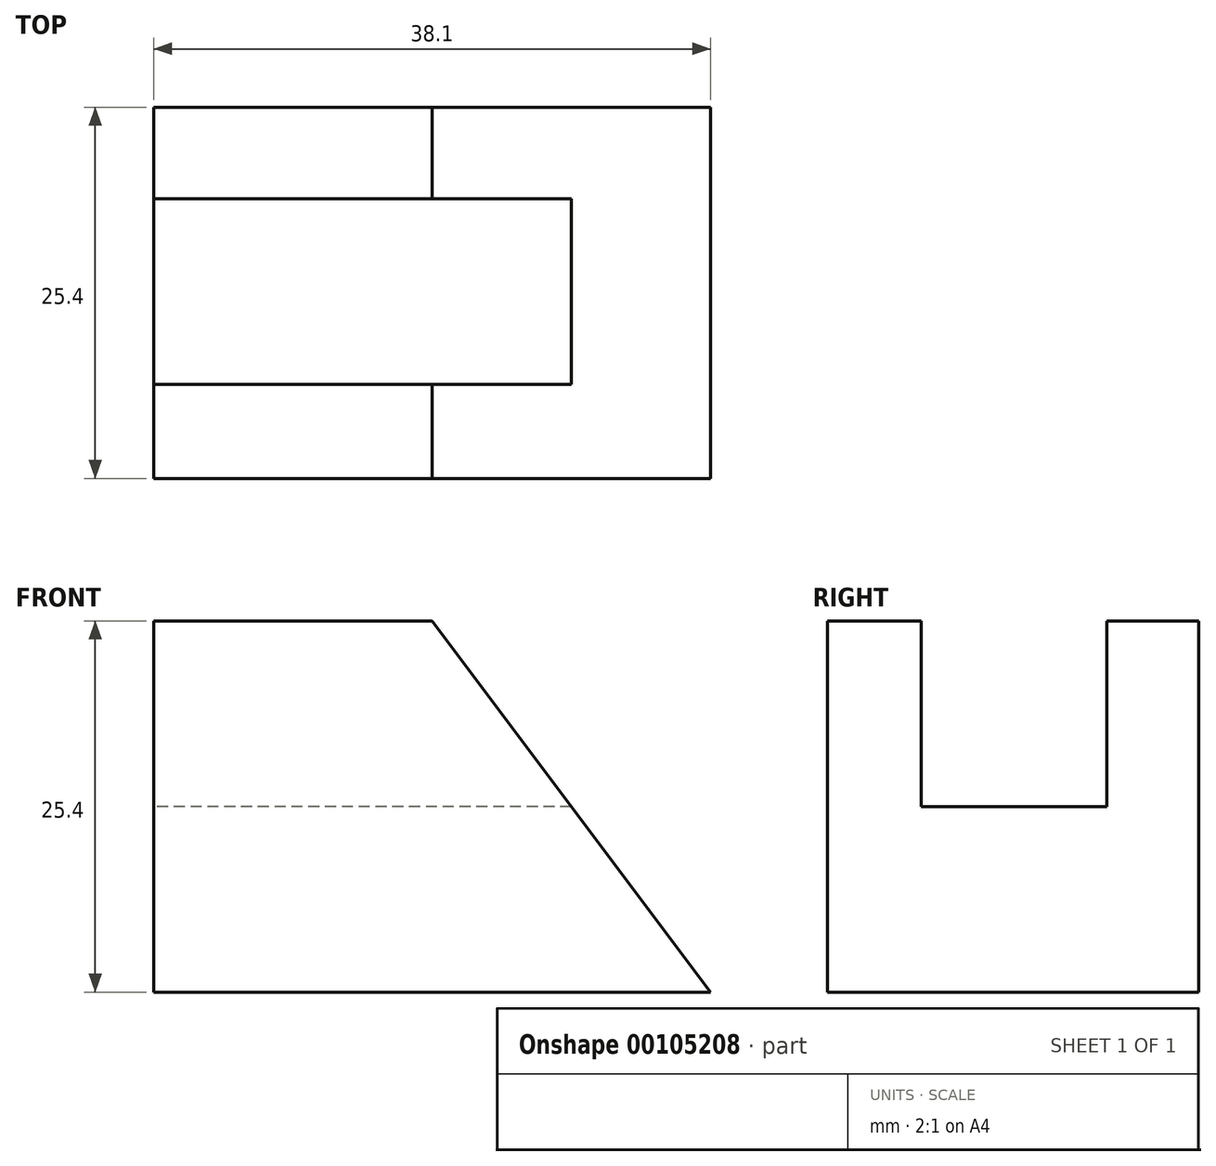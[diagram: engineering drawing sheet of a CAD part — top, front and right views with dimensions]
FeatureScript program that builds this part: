
annotation { "Feature Type Name" : "Feature", "Feature Type Description" : "" }
export const myFeature = defineFeature(function(context is Context, id is Id, definition is map)
    precondition{}
    {
        {
            var Q0;
            Q0=qCreatedBy(makeId("Top.planeOp"),FACE);
            var sketch = newSketch(context, id + "F0", { "sketchPlane" : qUnion([Q0])});
            skLineSegment(sketch, "E0", {"start": v(0, 0) * mm, "end": v(0, 25.4) * mm});
            skLineSegment(sketch, "E1", {"start": v(0, 25.4) * mm, "end": v(19.05, 25.4) * mm});
            skLineSegment(sketch, "E2", {"start": v(19.05, 25.4) * mm, "end": v(38.1, 25.4) * mm});
            skLineSegment(sketch, "E3", {"start": v(38.1, 25.4) * mm, "end": v(38.1, 0) * mm});
            skLineSegment(sketch, "E4", {"start": v(38.1, 0) * mm, "end": v(19.05, 0) * mm});
            skLineSegment(sketch, "E5", {"start": v(19.05, 0) * mm, "end": v(0, 0) * mm});
            skLineSegment(sketch, "E6", {"start": v(19.05, 25.4) * mm, "end": v(19.05, 19.13) * mm});
            skLineSegment(sketch, "E7", {"start": v(19.05, 0) * mm, "end": v(19.05, 6.43) * mm});
            skLineSegment(sketch, "E8", {"start": v(0, 6.43) * mm, "end": v(19.05, 6.43) * mm});
            skLineSegment(sketch, "E9", {"start": v(19.05, 6.43) * mm, "end": v(28.58, 6.43) * mm});
            skLineSegment(sketch, "E10", {"start": v(28.58, 6.43) * mm, "end": v(28.58, 19.13) * mm});
            skLineSegment(sketch, "E11", {"start": v(28.58, 19.13) * mm, "end": v(19.05, 19.13) * mm});
            skLineSegment(sketch, "E12", {"start": v(19.05, 19.13) * mm, "end": v(0, 19.13) * mm});
            skSolve(sketch);
        }
        {
            var Q0;
            {var subQ0=sQuery(id+"F0.wireOp",EDGE,"E1");Q0=makeQuery(id+"F0.imprint","IMPRINT",FACE,{"disambiguationData":[TD([[makeQuery(id+"F0.imprint","IMPRINT",EDGE,{"derivedFrom":subQ0}),-1.0]])]});}
            extrude(context, id + "F1", {"entities" : qUnion([Q0]), "depth" : 25.4 * mm});
        }
        {
            var Q0;
            {var subQ0=sQuery(id+"F0.wireOp",EDGE,"E5");Q0=makeQuery(id+"F0.imprint","IMPRINT",FACE,{"disambiguationData":[TD([[makeQuery(id+"F0.imprint","IMPRINT",EDGE,{"derivedFrom":subQ0}),-1.0]])]});}
            extrude(context, id + "F2", {"entities" : qUnion([Q0]), "depth" : 25.4 * mm});
        }
        {
            var Q0;
            {var subQ0=sQuery(id+"F0.wireOp",EDGE,"E8");Q0=makeQuery(id+"F0.imprint","IMPRINT",FACE,{"disambiguationData":[TD([[makeQuery(id+"F0.imprint","IMPRINT",EDGE,{"derivedFrom":subQ0}),1.0]])]});}
            var Q1;
            Q1=makeQuery(id+"F0.imprint","IMPRINT",FACE,{"disambiguationData":[TD([[makeQuery(id+"F0.imprint","IMPRINT",EDGE,{"derivedFrom":sQuery(id+"F0.wireOp",EDGE,"E2")}),-1.0]])]});
            extrude(context, id + "F3", {"entities" : qUnion([Q0, Q1]), "depth" : 12.7 * mm});
        }
        {
            var Q0;
            Q0=qCreatedBy(makeId("Front.planeOp"),FACE);
            var sketch = newSketch(context, id + "F4", { "sketchPlane" : qUnion([Q0])});
            skLineSegment(sketch, "E13", {"start": v(19.05, 0) * mm, "end": v(19.05, 25.4) * mm});
            skLineSegment(sketch, "E14", {"start": v(19.05, 25.4) * mm, "end": v(38.1, 0) * mm});
            skLineSegment(sketch, "E15", {"start": v(38.1, 0) * mm, "end": v(19.05, 0) * mm});
            skSolve(sketch);
        }
        {
            var Q0;
            Q0=makeQuery(id+"F4.imprint","IMPRINT",FACE,{"disambiguationData":[TD([[makeQuery(id+"F4.imprint","IMPRINT",EDGE,{"derivedFrom":sQuery(id+"F4.wireOp",EDGE,"E13")}),-1.0]])]});
            extrude(context, id + "F5", {"entities" : qUnion([Q0]), "operationType" : NewBodyOperationType.ADD, "oppositeDirection" : true, "depth" : 25.4 * mm});
        }
        {
            var Q0;
            Q0=qCreatedBy(makeId("Right.planeOp"),FACE);
            var sketch = newSketch(context, id + "F6", { "sketchPlane" : qUnion([Q0])});
            skLineSegment(sketch, "E16.bottom", {"start": v(19.13, 25.4) * mm, "end": v(6.43, 25.4) * mm});
            skLineSegment(sketch, "E16.top", {"start": v(19.13, 12.7) * mm, "end": v(6.43, 12.7) * mm});
            skLineSegment(sketch, "E16.left", {"start": v(19.13, 25.4) * mm, "end": v(19.13, 12.7) * mm});
            skLineSegment(sketch, "E16.right", {"start": v(6.43, 25.4) * mm, "end": v(6.43, 12.7) * mm});
            skSolve(sketch);
        }
        {
            var Q0;
            Q0=makeQuery(id+"F6.imprint","IMPRINT",FACE,{"disambiguationData":[TD([[makeQuery(id+"F6.imprint","IMPRINT",EDGE,{"derivedFrom":sQuery(id+"F6.wireOp",EDGE,"E16.bottom")}),1.0]])]});
            extrude(context, id + "F7", {"entities" : qUnion([Q0]), "operationType" : NewBodyOperationType.REMOVE, "endBound" : BoundingType.THROUGH_ALL, "depth" : 25.4 * mm});
        }
        {
            var Q0;
            Q0=qCreatedBy(makeId("Front.planeOp"),FACE);
            var sketch = newSketch(context, id + "F8", { "sketchPlane" : qUnion([Q0])});
            skLineSegment(sketch, "E17", {"start": v(38.1, 12.7) * mm, "end": v(38.1, 0) * mm});
            skLineSegment(sketch, "E18", {"start": v(38.1, 0) * mm, "end": v(28.58, 12.7) * mm});
            skLineSegment(sketch, "E19", {"start": v(28.58, 12.7) * mm, "end": v(38.1, 12.7) * mm});
            skSolve(sketch);
        }
        {
            var Q0;
            Q0=makeQuery(id+"F8.imprint","IMPRINT",FACE,{"disambiguationData":[TD([[makeQuery(id+"F8.imprint","IMPRINT",EDGE,{"derivedFrom":sQuery(id+"F8.wireOp",EDGE,"E17")}),-1.0]])]});
            extrude(context, id + "F9", {"entities" : qUnion([Q0]), "operationType" : NewBodyOperationType.REMOVE, "endBound" : BoundingType.THROUGH_ALL, "oppositeDirection" : true, "depth" : 25.4 * mm});
        }
    });
